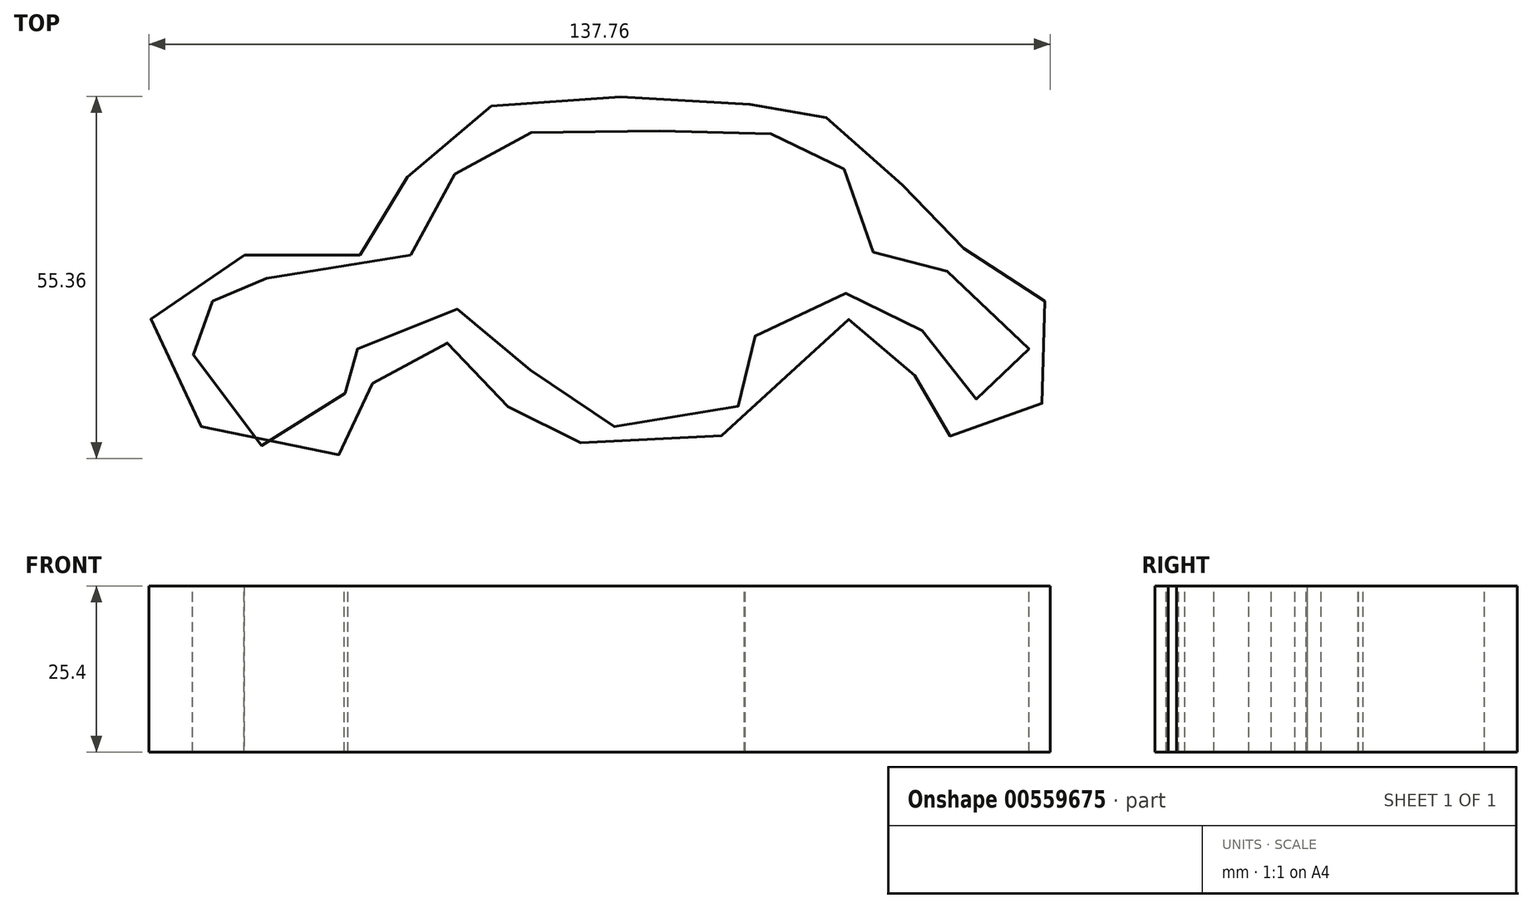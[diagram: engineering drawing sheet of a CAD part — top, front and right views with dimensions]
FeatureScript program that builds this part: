
annotation { "Feature Type Name" : "Feature", "Feature Type Description" : "" }
export const myFeature = defineFeature(function(context is Context, id is Id, definition is map)
    precondition{}
    {
        {
            var Q0;
            Q0=qCreatedBy(makeId("Top.planeOp"),FACE);
            var sketch = newSketch(context, id + "F0", { "sketchPlane" : qUnion([Q0])});
            skFitSpline(sketch, "E0", {"points": [v(-49.68, 0) * mm, v(-31.94, 0) * mm, v(-31.63, 0) * mm, v(-22.76, 15) * mm, v(-9.9, 23.26) * mm, v(15.18, 23.88) * mm, v(32.62, 22.65) * mm, v(39.05, 21.12) * mm, v(50.06, 11.94) * mm, v(56.49, 2.46) * mm, v(69.95, -2.44) * mm, v(73.32, -17.12) * mm, v(69.03, -26) * mm, v(54.35, -26.3) * mm, v(52.82, -18.96) * mm, v(46.7, -11) * mm, v(35.38, -11.92) * mm, v(30.79, -25.39) * mm, v(12.43, -27.53) * mm, v(-7.46, -27.83) * mm, v(-11.13, -17.74) * mm, v(-22.15, -13.45) * mm, v(-30.1, -19.57) * mm, v(-31.94, -28.75) * mm, v(-54.27, -27.53) * mm, v(-64.07, -10.09) * mm, v(-49.68, 0) * mm]});
            skSolve(sketch);
        }
        {
            var Q0;
            Q0=makeQuery(id+"F0.imprint","IMPRINT",FACE,{"disambiguationData":[TD([[makeQuery(id+"F0.imprint","IMPRINT",EDGE,{"derivedFrom":sQuery(id+"F0.wireOp",EDGE,"E0")}),-1.0]])]});
            var sketch = newSketch(context, id + "F1", { "sketchPlane" : qUnion([Q0])});
            skFitSpline(sketch, "E1", {"points": [v(-24.3, 0) * mm, v(-17.55, 12.41) * mm, v(-7.12, 18.55) * mm, v(19.56, 18.85) * mm, v(35.51, 17.63) * mm, v(43.8, 9.96) * mm, v(46.55, 0) * mm, v(46.86, 0) * mm, v(66.49, -7.22) * mm, v(68.64, -19.49) * mm, v(59.44, -21.02) * mm, v(51.77, -8.44) * mm, v(38.58, -6.6) * mm, v(26.92, -14.88) * mm, v(25.7, -23.17) * mm, v(0, -24.4) * mm, v(-8.65, -13.35) * mm, v(-24.3, -8.75) * mm, v(-34.42, -16.72) * mm, v(-34.11, -16.72) * mm, v(-37.48, -26.85) * mm, v(-54.97, -24.09) * mm, v(-57.11, -7.83) * mm, v(-56.8, -7.83) * mm, v(-49.75, -4.15) * mm, v(-49.75, -3.84) * mm, v(-24.3, 0) * mm]});
            skCircle(sketch, "E2", {"center": v(-20.61, -22.55) * mm, "radius": 6.59 * mm});
            skCircle(sketch, "E3", {"center": v(44.1, -20.4) * mm, "radius": 7.37 * mm});
            skSolve(sketch);
        }
        {
            var Q0;
            Q0=sQuery(id+"F1.wireOp",EDGE,"E1");
            var Q1;
            Q1=sQuery(id+"F0.wireOp",EDGE,"E0");
            extrude(context, id + "F2", {"bodyType" : ToolBodyType.SURFACE, "surfaceEntities" : qUnion([Q0, Q1]), "depth" : 25.4 * mm, "offsetDistance" : 25.4 * mm});
        }
    });
